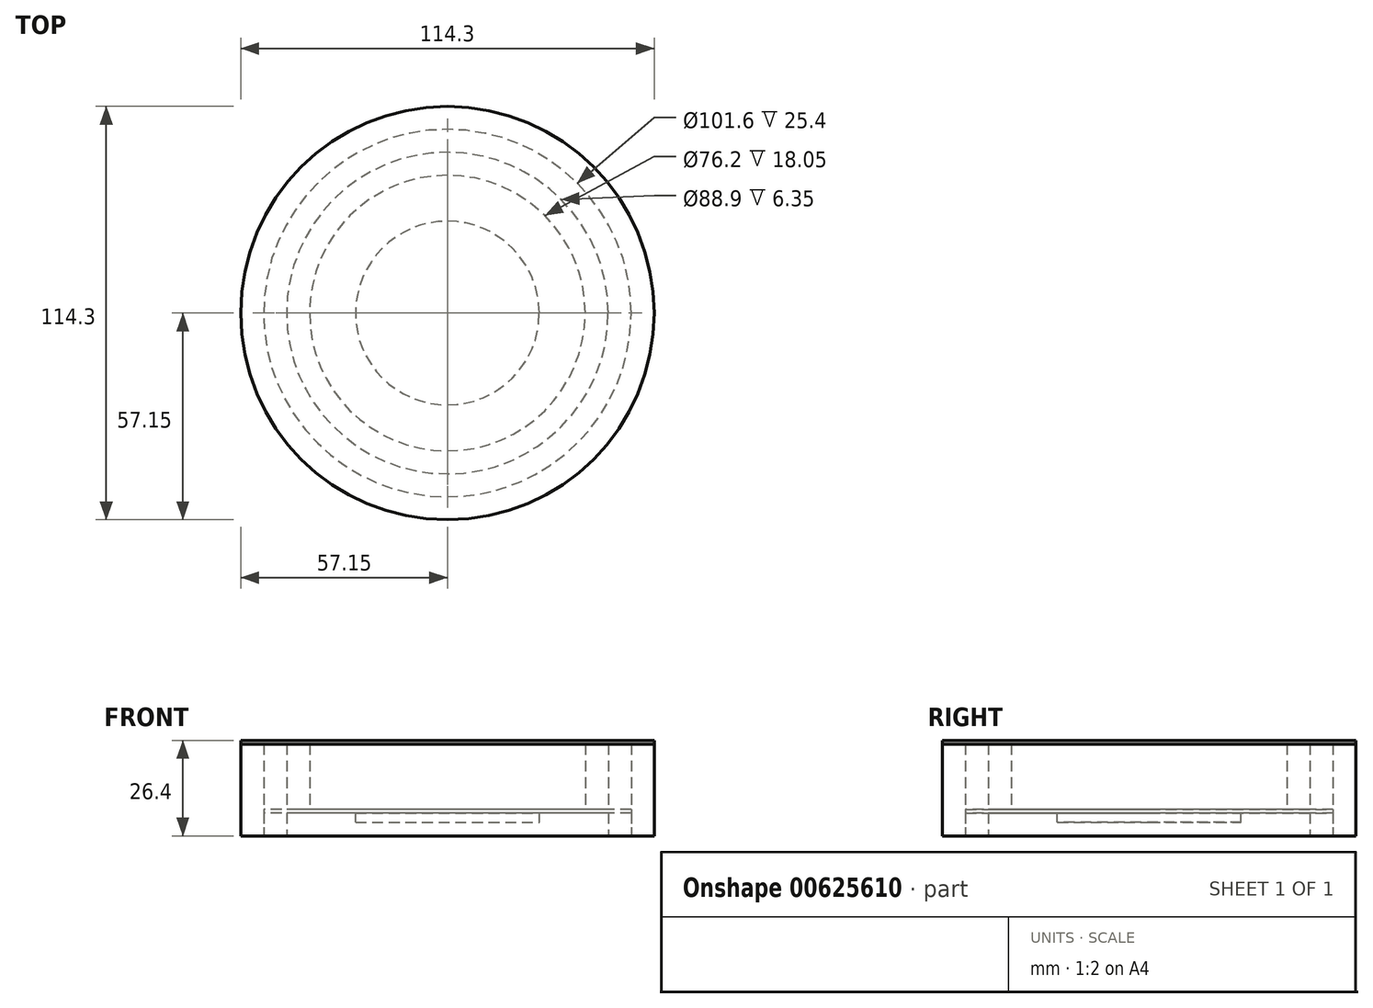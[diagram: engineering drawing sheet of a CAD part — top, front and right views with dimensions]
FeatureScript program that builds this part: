
annotation { "Feature Type Name" : "Feature", "Feature Type Description" : "" }
export const myFeature = defineFeature(function(context is Context, id is Id, definition is map)
    precondition{}
    {
        {
            var Q0;
            Q0=qCreatedBy(makeId("Top.planeOp"),FACE);
            var sketch = newSketch(context, id + "F0", { "sketchPlane" : qUnion([Q0])});
            skCircle(sketch, "E0", {"center": v(0, 0) * mm, "radius": 44.45 * mm});
            skCircle(sketch, "E1", {"center": v(0, 0) * mm, "radius": 50.8 * mm});
            skSolve(sketch);
        }
        {
            var Q0;
            Q0 = qSketchRegion(id + "F0", true);
            extrude(context, id + "F1", {"entities" : qUnion([Q0]), "depth" : 6.35 * mm, "offsetDistance" : 25.4 * mm});
        }
        {
            var Q0;
            Q0=qCreatedBy(makeId("Top.planeOp"),FACE);
            var sketch = newSketch(context, id + "F2", { "sketchPlane" : qUnion([Q0])});
            skCircle(sketch, "E2", {"center": v(0, 0) * mm, "radius": 57.15 * mm});
            skCircle(sketch, "E3", {"center": v(0, 0) * mm, "radius": 50.8 * mm});
            skSolve(sketch);
        }
        {
            var Q0;
            Q0=makeQuery(id+"F2.imprint","IMPRINT",FACE,{"disambiguationData":[TD([[makeQuery(id+"F2.imprint","IMPRINT",EDGE,{"derivedFrom":sQuery(id+"F2.wireOp",EDGE,"E2")}),1.0]])]});
            extrude(context, id + "F3", {"entities" : qUnion([Q0]), "depth" : 25.4 * mm, "offsetDistance" : 25.4 * mm});
        }
        {
            var Q0;
            Q0=makeQuery(id+"F1.opExtrude","CAP_FACE",FACE,{"disambiguationData":[OSD([sQuery(id+"F0.wireOp",EDGE,"E0"),sQuery(id+"F0.wireOp",EDGE,"E1")])],"isStart":false});
            var sketch = newSketch(context, id + "F4", { "sketchPlane" : qUnion([Q0])});
            skCircle(sketch, "E4", {"center": v(0, 0) * mm, "radius": 50.8 * mm});
            skSolve(sketch);
        }
        {
            var Q0;
            Q0 = qSketchRegion(id + "F4", true);
            extrude(context, id + "F5", {"entities" : qUnion([Q0]), "depth" : 1 * mm, "offsetDistance" : 25.4 * mm});
        }
        {
            var Q0;
            Q0=makeQuery(id+"F5.opExtrude","CAP_FACE",FACE,{"disambiguationData":[OSD([sQuery(id+"F4.wireOp",EDGE,"E4")])],"isStart":false});
            var sketch = newSketch(context, id + "F6", { "sketchPlane" : qUnion([Q0])});
            skCircle(sketch, "E5", {"center": v(0, 0) * mm, "radius": 44.45 * mm});
            skCircle(sketch, "E6", {"center": v(0, 0) * mm, "radius": 38.1 * mm});
            skSolve(sketch);
        }
        {
            var Q0;
            Q0=makeQuery(id+"F6.imprint","IMPRINT",FACE,{"disambiguationData":[TD([[makeQuery(id+"F6.imprint","IMPRINT",EDGE,{"derivedFrom":sQuery(id+"F6.wireOp",EDGE,"E5")}),1.0]])]});
            extrude(context, id + "F7", {"entities" : qUnion([Q0]), "depth" : 19.05 * mm - 1 * mm, "offsetDistance" : 25.4 * mm});
        }
        {
            var Q0;
            Q0=makeQuery(id+"F3.opExtrude","CAP_FACE",FACE,{"disambiguationData":[OSD([sQuery(id+"F2.wireOp",EDGE,"E2"),sQuery(id+"F2.wireOp",EDGE,"E3")])],"isStart":false});
            var sketch = newSketch(context, id + "F8", { "sketchPlane" : qUnion([Q0])});
            skCircle(sketch, "E7", {"center": v(0, 0) * mm, "radius": 57.15 * mm});
            skSolve(sketch);
        }
        {
            var Q0;
            Q0 = qSketchRegion(id + "F8", true);
            extrude(context, id + "F9", {"entities" : qUnion([Q0]), "depth" : 1 * mm, "offsetDistance" : 25.4 * mm});
        }
        {
            var Q0;
            Q0=makeQuery(id+"F5.opExtrude","CAP_FACE",FACE,{"disambiguationData":[OSD([sQuery(id+"F4.wireOp",EDGE,"E4")])],"isStart":true});
            var sketch = newSketch(context, id + "F10", { "sketchPlane" : qUnion([Q0])});
            skCircle(sketch, "E8", {"center": v(0, 0) * mm, "radius": 25.4 * mm});
            skSolve(sketch);
        }
        {
            var Q0;
            Q0=makeQuery(id+"F10.imprint","IMPRINT",FACE,{"disambiguationData":[TD([[makeQuery(id+"F10.imprint","IMPRINT",EDGE,{"derivedFrom":sQuery(id+"F10.wireOp",EDGE,"E8")}),1.0]])]});
            extrude(context, id + "F11", {"entities" : qUnion([Q0]), "depth" : 2.54 * mm, "offsetDistance" : 25.4 * mm});
        }
    });
